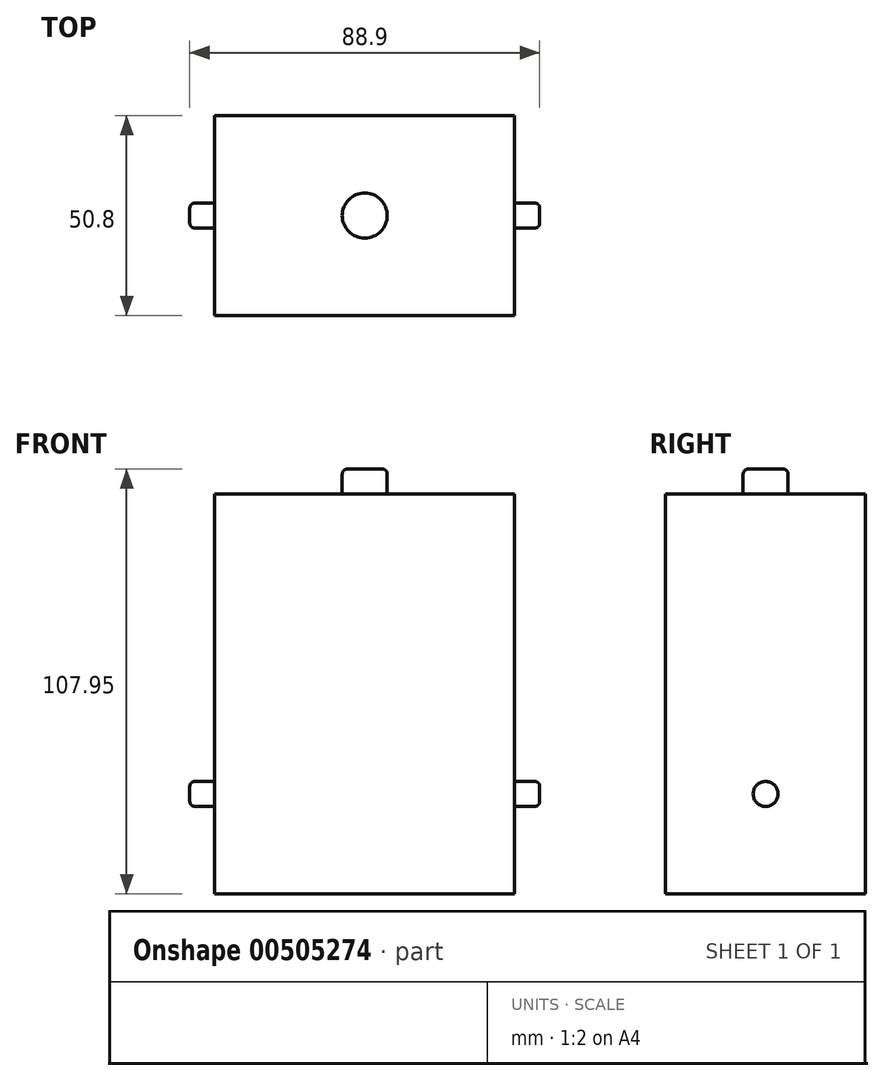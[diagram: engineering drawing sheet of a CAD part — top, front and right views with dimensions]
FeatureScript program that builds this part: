
annotation { "Feature Type Name" : "Feature", "Feature Type Description" : "" }
export const myFeature = defineFeature(function(context is Context, id is Id, definition is map)
    precondition{}
    {
        {
            var Q0;
            Q0=qCreatedBy(makeId("Front.planeOp"),FACE);
            var sketch = newSketch(context, id + "F0", { "sketchPlane" : qUnion([Q0])});
            skLineSegment(sketch, "E0.bottom", {"start": v(38.1, 50.8) * mm, "end": v(-38.1, 50.8) * mm});
            skLineSegment(sketch, "E0.top", {"start": v(38.1, -50.8) * mm, "end": v(-38.1, -50.8) * mm});
            skLineSegment(sketch, "E0.left", {"start": v(38.1, 50.8) * mm, "end": v(38.1, -50.8) * mm});
            skLineSegment(sketch, "E0.right", {"start": v(-38.1, 50.8) * mm, "end": v(-38.1, -50.8) * mm});
            skPoint(sketch, "E0.middle", {"position": v(0, 0) * mm});
            skSolve(sketch);
        }
        {
            var Q0;
            Q0 = qSketchRegion(id + "F0", true);
            extrude(context, id + "F1", {"entities" : qUnion([Q0]), "depth" : 50.8 * mm});
        }
        {
            var Q0;
            Q0=makeQuery(id+"F1.opExtrude","SWEPT_FACE",FACE,{"disambiguationData":[OSD([sQuery(id+"F0.wireOp",EDGE,"E0.left")])]});
            var sketch = newSketch(context, id + "F2", { "sketchPlane" : qUnion([Q0])});
            skCircle(sketch, "E1", {"center": v(-25.4, -25.4) * mm, "radius": 3.18 * mm});
            skSolve(sketch);
        }
        {
            var Q0;
            Q0=makeQuery(id+"F1.opExtrude","SWEPT_FACE",FACE,{"disambiguationData":[OSD([sQuery(id+"F0.wireOp",EDGE,"E0.right")])]});
            var sketch = newSketch(context, id + "F3", { "sketchPlane" : qUnion([Q0])});
            skCircle(sketch, "E2", {"center": v(25.4, -25.4) * mm, "radius": 3.17 * mm});
            skSolve(sketch);
        }
        {
            var Q0;
            Q0=makeQuery(id+"F1.opExtrude","SWEPT_FACE",FACE,{"disambiguationData":[OSD([sQuery(id+"F0.wireOp",EDGE,"E0.bottom")])]});
            var sketch = newSketch(context, id + "F4", { "sketchPlane" : qUnion([Q0])});
            skCircle(sketch, "E3", {"center": v(0, -25.4) * mm, "radius": 5.72 * mm});
            skSolve(sketch);
        }
        {
            var Q0;
            Q0=makeQuery(id+"F3.imprint","IMPRINT",FACE,{"disambiguationData":[TD([[makeQuery(id+"F3.imprint","IMPRINT",EDGE,{"derivedFrom":sQuery(id+"F3.wireOp",EDGE,"E2")}),1.0]])]});
            extrude(context, id + "F5", {"entities" : qUnion([Q0]), "operationType" : NewBodyOperationType.ADD, "depth" : 6.35 * mm});
        }
        {
            var Q0;
            Q0=makeQuery(id+"F2.imprint","IMPRINT",FACE,{"disambiguationData":[TD([[makeQuery(id+"F2.imprint","IMPRINT",EDGE,{"derivedFrom":sQuery(id+"F2.wireOp",EDGE,"E1")}),1.0]])]});
            extrude(context, id + "F6", {"entities" : qUnion([Q0]), "operationType" : NewBodyOperationType.ADD, "depth" : 6.35 * mm});
        }
        {
            var Q0;
            Q0=makeQuery(id+"F4.imprint","IMPRINT",FACE,{"disambiguationData":[TD([[makeQuery(id+"F4.imprint","IMPRINT",EDGE,{"derivedFrom":sQuery(id+"F4.wireOp",EDGE,"E3")}),1.0]])]});
            extrude(context, id + "F7", {"entities" : qUnion([Q0]), "operationType" : NewBodyOperationType.ADD, "depth" : 6.35 * mm});
        }
        {
            var Q0;
            Q0=makeQuery(id+"F6.opExtrude","CAP_EDGE",EDGE,{"disambiguationData":[OSD([sQuery(id+"F2.wireOp",EDGE,"E1")])],"isStart":false});
            var Q1;
            Q1=makeQuery(id+"F7.opExtrude","CAP_EDGE",EDGE,{"disambiguationData":[OSD([sQuery(id+"F4.wireOp",EDGE,"E3")])],"isStart":false});
            var Q2;
            Q2=makeQuery(id+"F5.opExtrude","CAP_EDGE",EDGE,{"disambiguationData":[OSD([sQuery(id+"F3.wireOp",EDGE,"E2")])],"isStart":false});
            fillet(context, id + "F8", {"entities" : qUnion([Q0, Q1, Q2]), "radius" : 1.27 * mm, "tangentPropagation" : true, "allowEdgeOverflow" : false});
        }
    });
